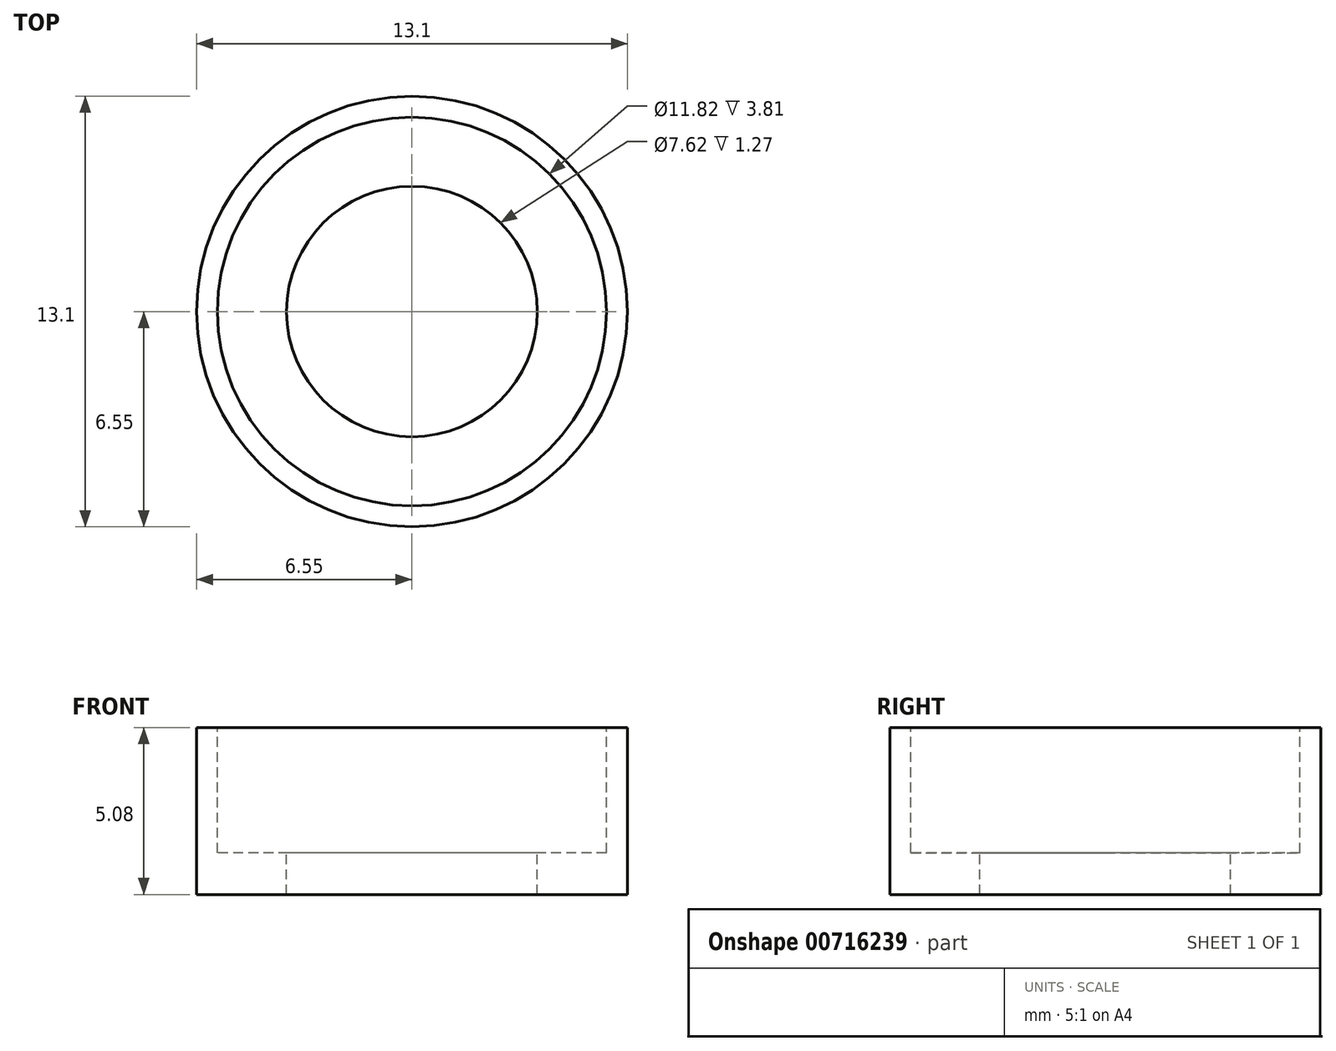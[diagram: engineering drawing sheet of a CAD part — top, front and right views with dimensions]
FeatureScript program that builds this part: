
annotation { "Feature Type Name" : "Feature", "Feature Type Description" : "" }
export const myFeature = defineFeature(function(context is Context, id is Id, definition is map)
    precondition{}
    {
        {
            var Q0;
            Q0=qCreatedBy(makeId("Front.planeOp"),FACE);
            var sketch = newSketch(context, id + "F0", { "sketchPlane" : qUnion([Q0])});
            skLineSegment(sketch, "E0.bottom", {"start": v(-6.15, 1.27) * mm, "end": v(6.55, 1.27) * mm});
            skLineSegment(sketch, "E0.top", {"start": v(-6.15, 0) * mm, "end": v(6.55, 0) * mm});
            skLineSegment(sketch, "E0.left", {"start": v(-6.15, 1.27) * mm, "end": v(-6.15, 0) * mm});
            skLineSegment(sketch, "E0.right", {"start": v(6.55, 1.27) * mm, "end": v(6.55, 0) * mm});
            skLineSegment(sketch, "E1.bottom", {"start": v(-3.81, 1.27) * mm, "end": v(3.81, 1.27) * mm});
            skLineSegment(sketch, "E1.top", {"start": v(-3.81, 0) * mm, "end": v(3.81, 0) * mm});
            skLineSegment(sketch, "E1.left", {"start": v(-3.81, 1.27) * mm, "end": v(-3.81, 0) * mm});
            skLineSegment(sketch, "E1.right", {"start": v(3.81, 1.27) * mm, "end": v(3.81, 0) * mm});
            skLineSegment(sketch, "E2.bottom", {"start": v(-6.15, 5.08) * mm, "end": v(-5.51, 5.08) * mm});
            skLineSegment(sketch, "E2.top", {"start": v(-6.15, 1.27) * mm, "end": v(-5.51, 1.27) * mm});
            skLineSegment(sketch, "E2.left", {"start": v(-6.15, 5.08) * mm, "end": v(-6.15, 1.27) * mm});
            skLineSegment(sketch, "E2.right", {"start": v(-5.51, 5.08) * mm, "end": v(-5.51, 1.27) * mm});
            skLineSegment(sketch, "E3.bottom", {"start": v(6.55, 1.27) * mm, "end": v(5.91, 1.27) * mm});
            skLineSegment(sketch, "E3.top", {"start": v(6.55, 5.08) * mm, "end": v(5.91, 5.08) * mm});
            skLineSegment(sketch, "E3.left", {"start": v(6.55, 1.27) * mm, "end": v(6.55, 5.08) * mm});
            skLineSegment(sketch, "E3.right", {"start": v(5.91, 1.27) * mm, "end": v(5.91, 5.08) * mm});
            skLineSegment(sketch, "E4", {"start": v(0, 1.27) * mm, "end": v(0, 0) * mm});
            skSolve(sketch);
        }
        {
            var Q0;
            {var subQ0=sQuery(id+"F0.wireOp",EDGE,"E0.right");Q0=makeQuery(id+"F0.imprint","IMPRINT",FACE,{"disambiguationData":[TD([[makeQuery(id+"F0.imprint","IMPRINT",EDGE,{"derivedFrom":subQ0}),-1.0]])]});}
            var Q1;
            Q1=makeQuery(id+"F0.imprint","IMPRINT",FACE,{"disambiguationData":[TD([[makeQuery(id+"F0.imprint","IMPRINT",EDGE,{"derivedFrom":sQuery(id+"F0.wireOp",EDGE,"E3.top")}),1.0]])]});
            var Q2;
            Q2=sQuery(id+"F0.wireOp",EDGE,"E4");
            revolve(context, id + "F1", {"surfaceOperationType" : NewSurfaceOperationType.NEW, "entities" : qUnion([Q0, Q1]), "axis" : qUnion([Q2]), "revolveType" : RevolveType.FULL});
        }
    });
